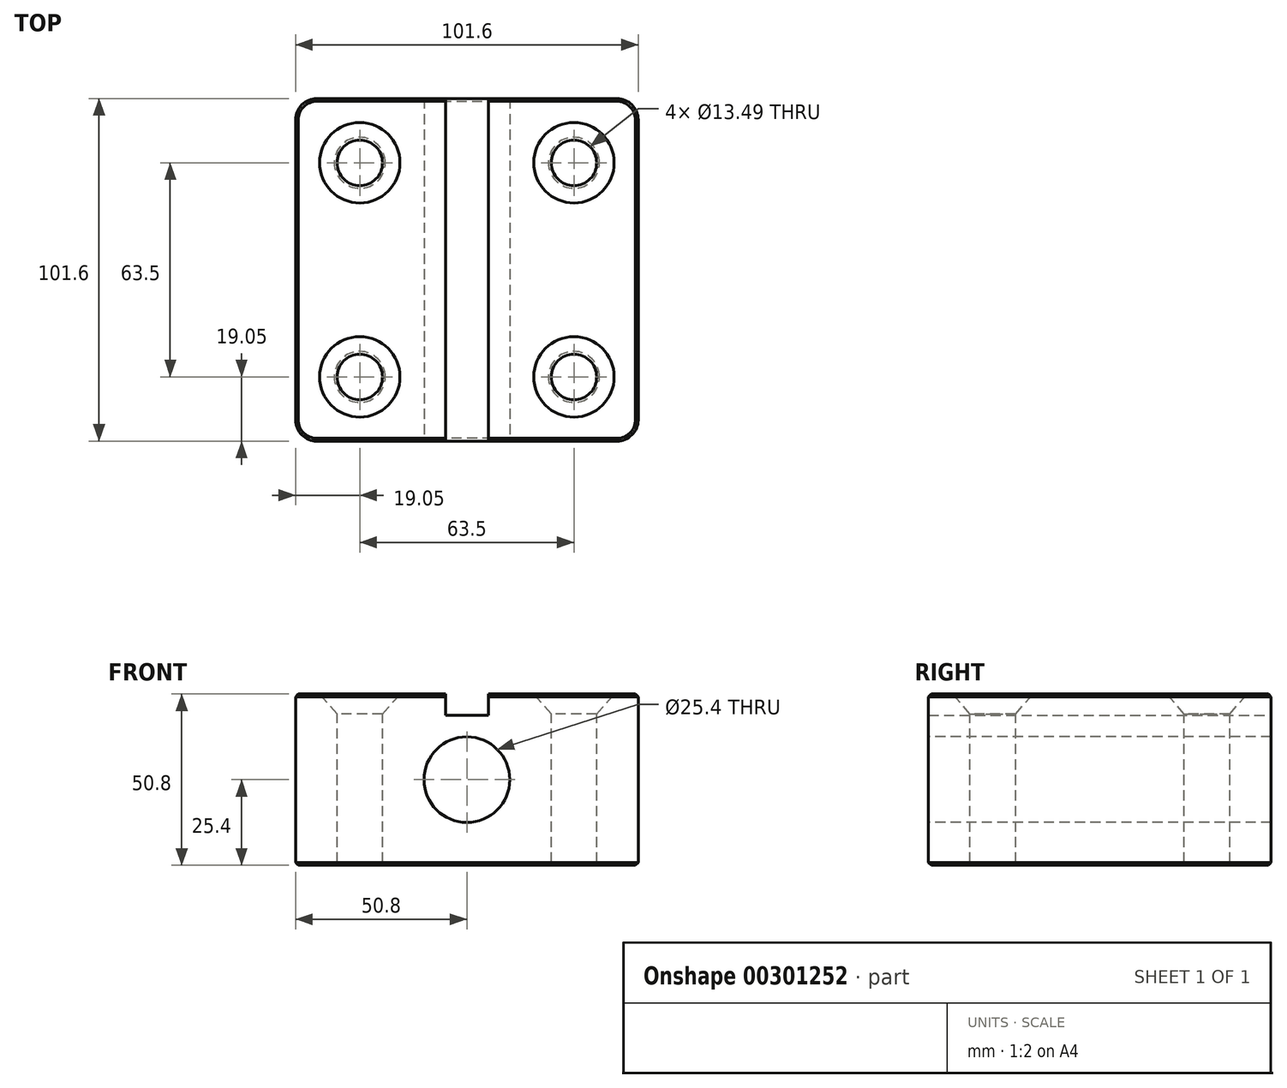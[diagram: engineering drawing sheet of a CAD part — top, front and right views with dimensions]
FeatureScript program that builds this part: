
annotation { "Feature Type Name" : "Feature", "Feature Type Description" : "" }
export const myFeature = defineFeature(function(context is Context, id is Id, definition is map)
    precondition{}
    {
        {
            var Q0;
            Q0=qCreatedBy(makeId("Front.planeOp"),FACE);
            var sketch = newSketch(context, id + "F0", { "sketchPlane" : qUnion([Q0])});
            skLineSegment(sketch, "E0.bottom", {"start": v(-50.8, 25.4) * mm, "end": v(50.8, 25.4) * mm});
            skLineSegment(sketch, "E0.top", {"start": v(-50.8, -25.4) * mm, "end": v(50.8, -25.4) * mm});
            skLineSegment(sketch, "E0.left", {"start": v(-50.8, 25.4) * mm, "end": v(-50.8, -25.4) * mm});
            skLineSegment(sketch, "E0.right", {"start": v(50.8, 25.4) * mm, "end": v(50.8, -25.4) * mm});
            skLineSegment(sketch, "E1", {"start": v(0, 25.4) * mm, "end": v(0, 19.05) * mm});
            skPoint(sketch, "E1.endSnap0", {"position": v(0, 25.4) * mm});
            skLineSegment(sketch, "E2", {"start": v(0, 19.05) * mm, "end": v(6.35, 19.05) * mm});
            skLineSegment(sketch, "E3", {"start": v(6.35, 19.05) * mm, "end": v(6.35, 25.4) * mm});
            skLineSegment(sketch, "E4.MirrorCS", {"start": v(0, 19.05) * mm, "end": v(-6.35, 19.05) * mm});
            skLineSegment(sketch, "E5.MirrorCS", {"start": v(-6.35, 19.05) * mm, "end": v(-6.35, 25.4) * mm});
            skSolve(sketch);
        }
        {
            var Q0;
            Q0=makeQuery(id+"F0.imprint","IMPRINT",FACE,{"disambiguationData":[TD([[makeQuery(id+"F0.imprint","IMPRINT",EDGE,{"derivedFrom":sQuery(id+"F0.wireOp",EDGE,"E0.bottom")}),-1.0]])]});
            extrude(context, id + "F1", {"entities" : qUnion([Q0]), "endBound" : BoundingType.SYMMETRIC, "depth" : 101.6 * mm});
        }
        {
            var Q0;
            Q0=makeQuery(id+"F1.opExtrude","SWEPT_FACE",FACE,{"disambiguationData":[OSD([sQuery(id+"F0.wireOp",EDGE,"E0.bottom")])]});
            var sketch = newSketch(context, id + "F2", { "sketchPlane" : qUnion([Q0])});
            skPoint(sketch, "E6", {"position": v(-31.75, 31.75) * mm});
            skPoint(sketch, "E7.MirrorP", {"position": v(31.75, 31.75) * mm});
            skPoint(sketch, "E8.MirrorP", {"position": v(-31.75, -31.75) * mm});
            skPoint(sketch, "E9.MirrorP", {"position": v(31.75, -31.75) * mm});
            skSolve(sketch);
        }
        {
            var Q0;
            Q0=sQuery(id+"F2.wireOp",VERTEX,"E6");
            var Q1;
            Q1=sQuery(id+"F2.wireOp",VERTEX,"E7.MirrorP");
            var Q2;
            Q2=sQuery(id+"F2.wireOp",VERTEX,"E8.MirrorP");
            var Q3;
            Q3=sQuery(id+"F2.wireOp",VERTEX,"E9.MirrorP");
            var Q4;
            Q4=makeQuery(id+"F1.opExtrude","SWEPT_BODY",BODY,{"disambiguationData":[OSD([sQuery(id+"F0.wireOp",EDGE,"E0.bottom"),sQuery(id+"F0.wireOp",EDGE,"E0.top"),sQuery(id+"F0.wireOp",EDGE,"E0.left"),sQuery(id+"F0.wireOp",EDGE,"E0.right")])]});
            hole(context, id + "F3", {"style" : HoleStyle.C_SINK, "endStyle" : HoleEndStyle.THROUGH, "standardTappedOrClearance" : lookupTablePath({ "standard" : "ANSI", "fit" : "Normal (ASME)", "size" : "1/2", "type" : "Clearance" }), "standardBlindInLast" : lookupTablePath({ "fit" : "Free", "standard" : "ANSI", "size" : "1/2", "type" : "Clearance" }), "holeDiameter" : 13.5 * mm, "cSinkDiameter" : 23.83 * mm, "cSinkAngle" : 82 * degree, "tappedDepth" : 12.7 * mm, "tapClearance" : 3, "locations" : qUnion([Q0, Q1, Q2, Q3]), "scope" : qUnion([Q4])});
        }
        {
            var Q0;
            Q0=makeQuery(id+"F1.opExtrude","CAP_EDGE",EDGE,{"disambiguationData":[OSD([sQuery(id+"F0.wireOp",EDGE,"E0.left")])],"isStart":true});
            var Q1;
            Q1=makeQuery(id+"F1.opExtrude","CAP_EDGE",EDGE,{"disambiguationData":[OSD([sQuery(id+"F0.wireOp",EDGE,"E0.left")])],"isStart":false});
            var Q2;
            Q2=makeQuery(id+"F1.opExtrude","CAP_EDGE",EDGE,{"disambiguationData":[OSD([sQuery(id+"F0.wireOp",EDGE,"E0.right")])],"isStart":false});
            var Q3;
            Q3=makeQuery(id+"F1.opExtrude","CAP_EDGE",EDGE,{"disambiguationData":[OSD([sQuery(id+"F0.wireOp",EDGE,"E0.right")])],"isStart":true});
            fillet(context, id + "F4", {"entities" : qUnion([Q0, Q1, Q2, Q3]), "radius" : 6.35 * mm, "tangentPropagation" : true, "allowEdgeOverflow" : false});
        }
        {
            var Q0;
            Q0=makeQuery(id+"F1.opExtrude","SWEPT_EDGE",EDGE,{"disambiguationData":[OSD([sQuery(id+"F0.wireOp",EDGE,"E0.bottom"),sQuery(id+"F0.wireOp",EDGE,"E0.right")])]});
            var Q1;
            Q1=makeQuery(id+"F1.opExtrude","CAP_EDGE",EDGE,{"disambiguationData":[OSD([sQuery(id+"F0.wireOp",EDGE,"E0.bottom")])],"isStart":true});
            var Q2;
            Q2=makeQuery(id+"F1.opExtrude","SWEPT_EDGE",EDGE,{"disambiguationData":[OSD([sQuery(id+"F0.wireOp",EDGE,"E0.bottom"),sQuery(id+"F0.wireOp",EDGE,"E0.left")])]});
            var Q3;
            Q3=makeQuery(id+"F1.opExtrude","CAP_EDGE",EDGE,{"disambiguationData":[OSD([sQuery(id+"F0.wireOp",EDGE,"E0.bottom")])],"isStart":false});
            var Q4;
            Q4=makeQuery(id+"F1.opExtrude","SWEPT_FACE",FACE,{"disambiguationData":[OSD([sQuery(id+"F0.wireOp",EDGE,"E0.top")])]});
            chamfer(context, id + "F5", {"entities" : qUnion([Q0, Q1, Q2, Q3, Q4]), "width" : 0.81 * mm, "tangentPropagation" : true});
        }
        {
            var Q0;
            Q0=makeQuery(id+"F1.opExtrude","CAP_FACE",FACE,{"disambiguationData":[OSD([sQuery(id+"F0.wireOp",EDGE,"E0.bottom"),sQuery(id+"F0.wireOp",EDGE,"E0.top"),sQuery(id+"F0.wireOp",EDGE,"E0.left"),sQuery(id+"F0.wireOp",EDGE,"E0.right")])],"isStart":false});
            var sketch = newSketch(context, id + "F6", { "sketchPlane" : qUnion([Q0])});
            skPoint(sketch, "E10", {"position": v(0, 0) * mm});
            skSolve(sketch);
        }
        {
            var Q0;
            Q0=sQuery(id+"F6.wireOp",VERTEX,"E10");
            var Q1;
            Q1=makeQuery(id+"F1.opExtrude","SWEPT_BODY",BODY,{"disambiguationData":[OSD([sQuery(id+"F0.wireOp",EDGE,"E0.bottom"),sQuery(id+"F0.wireOp",EDGE,"E0.top"),sQuery(id+"F0.wireOp",EDGE,"E0.left"),sQuery(id+"F0.wireOp",EDGE,"E0.right")])]});
            hole(context, id + "F7", {"style" : HoleStyle.SIMPLE, "endStyle" : HoleEndStyle.THROUGH, "holeDiameter" : 25.4 * mm, "tappedDepth" : 12.7 * mm, "tapClearance" : 3, "locations" : qUnion([Q0]), "scope" : qUnion([Q1])});
        }
    });
